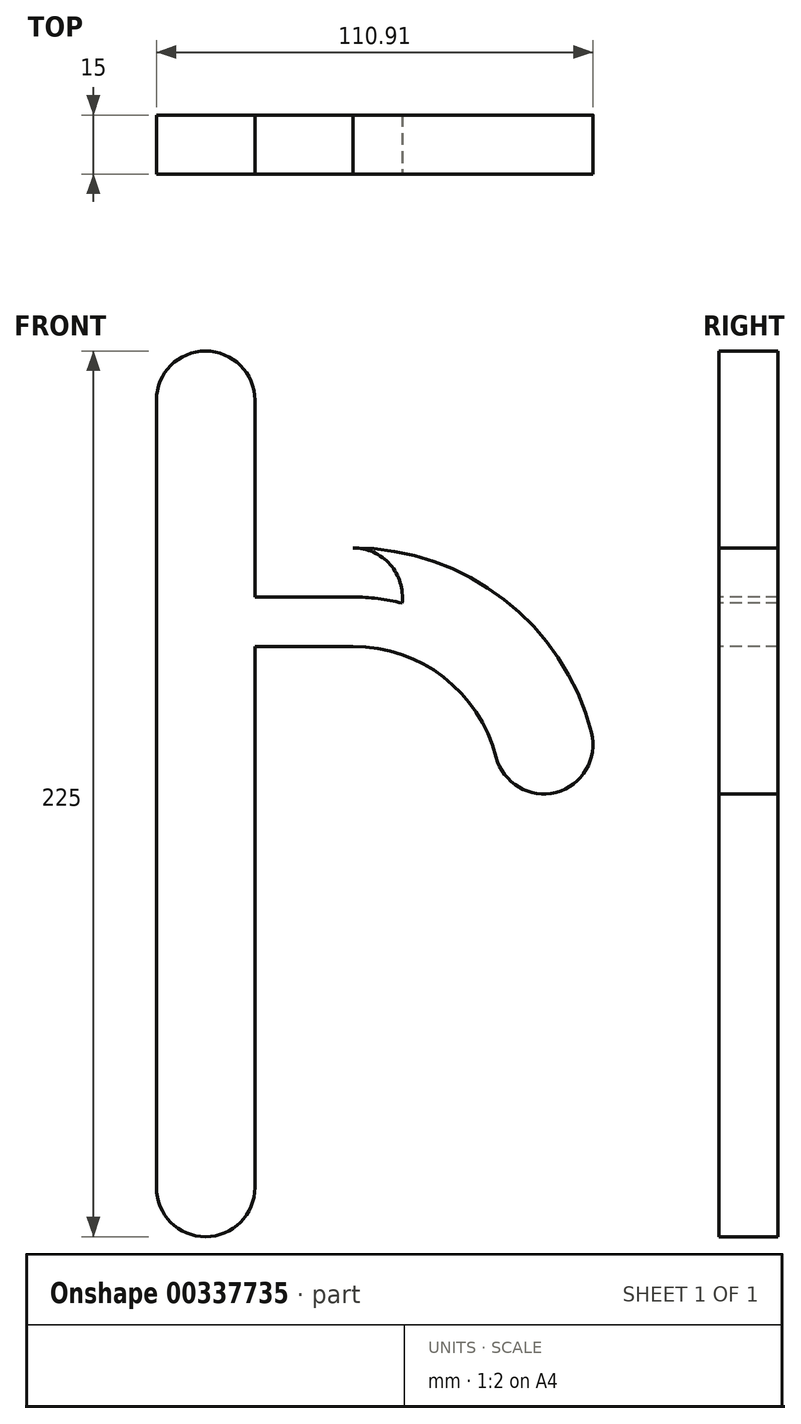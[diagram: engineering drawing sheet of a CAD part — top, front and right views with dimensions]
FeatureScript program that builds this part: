
annotation { "Feature Type Name" : "Feature", "Feature Type Description" : "" }
export const myFeature = defineFeature(function(context is Context, id is Id, definition is map)
    precondition{}
    {
        {
            var Q0;
            Q0=qCreatedBy(makeId("Front.planeOp"),FACE);
            var sketch = newSketch(context, id + "F0", { "sketchPlane" : qUnion([Q0])});
            skLineSegment(sketch, "E0.bottom", {"start": v(-12.5, 100) * mm, "end": v(12.5, 100) * mm});
            skLineSegment(sketch, "E0.top", {"start": v(-12.5, -100) * mm, "end": v(12.5, -100) * mm});
            skLineSegment(sketch, "E0.left", {"start": v(-12.5, 100) * mm, "end": v(-12.5, -100) * mm});
            skLineSegment(sketch, "E0.right", {"start": v(12.5, 100) * mm, "end": v(12.5, -100) * mm});
            skPoint(sketch, "E0.middle", {"position": v(0, 0) * mm});
            skCircle(sketch, "E1", {"center": v(0, 100) * mm, "radius": 12.5 * mm});
            skCircle(sketch, "E2", {"center": v(0, -100) * mm, "radius": 12.5 * mm});
            skArc(sketch, "E3", {"start": v(85.91, 12.5) * mm, "mid": v(68.12, 39.53) * mm, "end": v(37.5, 50) * mm});
            skLineSegment(sketch, "E4", {"start": v(-37.5, 50) * mm, "end": v(37.5, 50) * mm});
            skArc(sketch, "E5", {"start": v(-85.91, 87.5) * mm, "mid": v(-68.12, 60.47) * mm, "end": v(-37.5, 50) * mm});
            skLineSegment(sketch, "E6", {"start": v(-85.91, 87.5) * mm, "end": v(-62.5, 87.5) * mm, "construction": true});
            skLineSegment(sketch, "E7", {"start": v(12.5, 12.5) * mm, "end": v(85.91, 12.5) * mm, "construction": true});
            skArc(sketch, "E8.0.startCap", {"start": v(-98.02, 84.38) * mm, "mid": v(-89.04, 99.6) * mm, "end": v(-73.8, 90.62) * mm});
            skArc(sketch, "E8.0.left", {"start": v(-73.8, 90.62) * mm, "mid": v(-60.46, 70.35) * mm, "end": v(-37.5, 62.5) * mm});
            skArc(sketch, "E8.0.right", {"start": v(-98.02, 84.38) * mm, "mid": v(-75.77, 50.59) * mm, "end": v(-37.5, 37.5) * mm});
            skArc(sketch, "E9.0.startCap", {"start": v(98.02, 15.63) * mm, "mid": v(89.04, 0.4) * mm, "end": v(73.8, 9.38) * mm});
            skArc(sketch, "E9.0.left", {"start": v(73.8, 9.38) * mm, "mid": v(60.46, 29.65) * mm, "end": v(37.5, 37.5) * mm});
            skArc(sketch, "E9.0.right", {"start": v(98.02, 15.63) * mm, "mid": v(75.77, 49.41) * mm, "end": v(37.5, 62.5) * mm});
            skArc(sketch, "E10.0.endCap", {"start": v(37.5, 62.5) * mm, "mid": v(46.87, 58.27) * mm, "end": v(49.9, 48.44) * mm});
            skLineSegment(sketch, "E10.0.left", {"start": v(-37.5, 62.5) * mm, "end": v(37.5, 62.5) * mm});
            skLineSegment(sketch, "E10.0.right", {"start": v(-37.5, 37.5) * mm, "end": v(37.5, 37.5) * mm});
            skSolve(sketch);
        }
        {
            var Q0;
            {var subQ0=sQuery(id+"F0.wireOp",EDGE,"E0.top");Q0=makeQuery(id+"F0.imprint","IMPRINT",FACE,{"disambiguationData":[TD([[makeQuery(id+"F0.imprint","IMPRINT",EDGE,{"derivedFrom":subQ0}),-1.0]])]});}
            var Q1;
            {var subQ0=sQuery(id+"F0.wireOp",EDGE,"E0.top");Q1=makeQuery(id+"F0.imprint","IMPRINT",FACE,{"disambiguationData":[TD([[makeQuery(id+"F0.imprint","IMPRINT",EDGE,{"derivedFrom":subQ0}),1.0]])]});}
            var Q2;
            {var subQ1=sQuery(id+"F0.wireOp",EDGE,"E0.left");var subQ4=sQuery(id+"F0.wireOp",EDGE,"E10.0.right");var subQ5=makeQuery(id+"F0.imprint","INTERSECT",VERTEX,{"derivedFrom":[subQ1,subQ4]});Q2=makeQuery(id+"F0.imprint","IMPRINT",FACE,{"disambiguationData":[TD([[makeQuery(id+"F0.imprint","IMPRINT",EDGE,{"disambiguationData":[TD([[subQ5,-1.0]])],"derivedFrom":subQ4}),-1.0]])]});}
            var Q3;
            {var subQ0=sQuery(id+"F0.wireOp",EDGE,"E10.0.left");var subQ1=sQuery(id+"F0.wireOp",EDGE,"E0.left");var subQ2=makeQuery(id+"F0.imprint","INTERSECT",VERTEX,{"derivedFrom":[subQ1,subQ0]});Q3=makeQuery(id+"F0.imprint","IMPRINT",FACE,{"disambiguationData":[TD([[makeQuery(id+"F0.imprint","IMPRINT",EDGE,{"disambiguationData":[TD([[subQ2,-1.0]])],"derivedFrom":subQ1}),1.0]])]});}
            var Q4;
            {var subQ0=sQuery(id+"F0.wireOp",EDGE,"E4");var subQ1=sQuery(id+"F0.wireOp",EDGE,"E0.left");var subQ2=makeQuery(id+"F0.imprint","INTERSECT",VERTEX,{"derivedFrom":[subQ1,subQ0]});Q4=makeQuery(id+"F0.imprint","IMPRINT",FACE,{"disambiguationData":[TD([[makeQuery(id+"F0.imprint","IMPRINT",EDGE,{"disambiguationData":[TD([[subQ2,-1.0]])],"derivedFrom":subQ1}),1.0]])]});}
            var Q5;
            Q5=makeQuery(id+"F0.imprint","IMPRINT",FACE,{"disambiguationData":[TD([[makeQuery(id+"F0.imprint","IMPRINT",EDGE,{"derivedFrom":sQuery(id+"F0.wireOp",EDGE,"E8.0.startCap")}),-1.0]])]});
            var Q6;
            Q6=makeQuery(id+"F0.imprint","IMPRINT",FACE,{"disambiguationData":[TD([[makeQuery(id+"F0.imprint","IMPRINT",EDGE,{"derivedFrom":sQuery(id+"F0.wireOp",EDGE,"E9.0.startCap")}),-1.0]])]});
            var Q7;
            {var subQ0=sQuery(id+"F0.wireOp",EDGE,"E10.0.endCap");Q7=makeQuery(id+"F0.imprint","IMPRINT",FACE,{"disambiguationData":[TD([[makeQuery(id+"F0.imprint","IMPRINT",EDGE,{"derivedFrom":subQ0}),-1.0]])]});}
            var Q8;
            {var subQ1=sQuery(id+"F0.wireOp",EDGE,"E0.left");var subQ4=sQuery(id+"F0.wireOp",EDGE,"E10.0.left");var subQ5=makeQuery(id+"F0.imprint","INTERSECT",VERTEX,{"derivedFrom":[subQ1,subQ4]});Q8=makeQuery(id+"F0.imprint","IMPRINT",FACE,{"disambiguationData":[TD([[makeQuery(id+"F0.imprint","IMPRINT",EDGE,{"disambiguationData":[TD([[subQ5,-1.0]])],"derivedFrom":subQ4}),1.0]])]});}
            var Q9;
            {var subQ0=sQuery(id+"F0.wireOp",EDGE,"E0.bottom");Q9=makeQuery(id+"F0.imprint","IMPRINT",FACE,{"disambiguationData":[TD([[makeQuery(id+"F0.imprint","IMPRINT",EDGE,{"derivedFrom":subQ0}),-1.0]])]});}
            var Q10;
            {var subQ0=sQuery(id+"F0.wireOp",EDGE,"E0.bottom");Q10=makeQuery(id+"F0.imprint","IMPRINT",FACE,{"disambiguationData":[TD([[makeQuery(id+"F0.imprint","IMPRINT",EDGE,{"derivedFrom":subQ0}),1.0]])]});}
            extrude(context, id + "F1", {"entities" : qUnion([Q0, Q1, Q2, Q3, Q4, Q5, Q6, Q7, Q8, Q9, Q10]), "oppositeDirection" : true, "depth" : 15 * mm});
        }
    });
